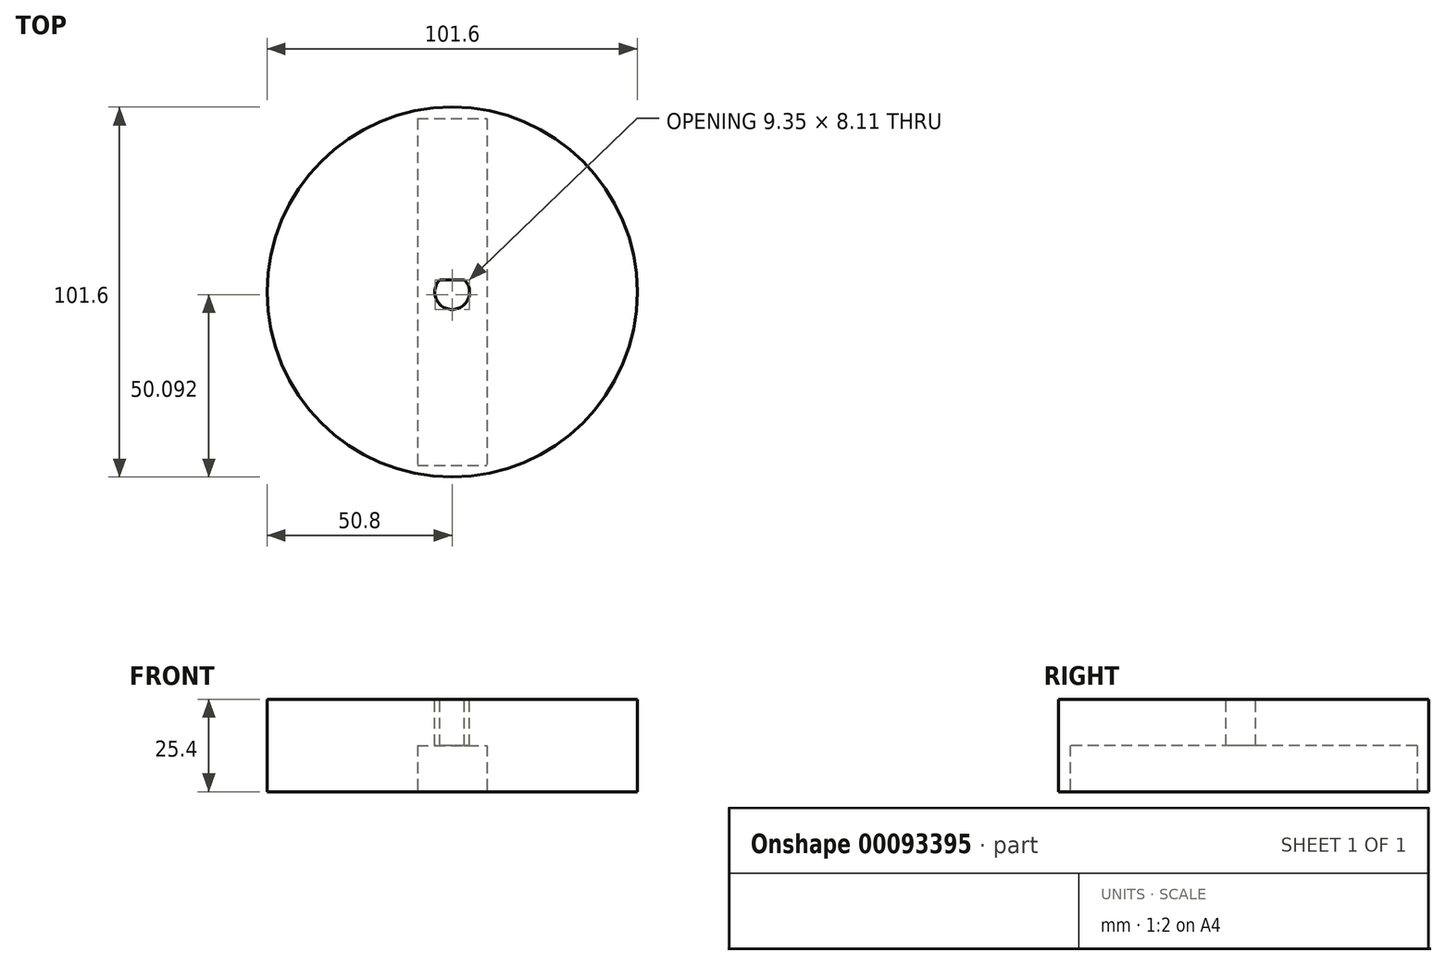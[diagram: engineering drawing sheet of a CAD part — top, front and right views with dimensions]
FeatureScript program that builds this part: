
annotation { "Feature Type Name" : "Feature", "Feature Type Description" : "" }
export const myFeature = defineFeature(function(context is Context, id is Id, definition is map)
    precondition{}
    {
        {
            var Q0;
            Q0=qCreatedBy(makeId("Top.planeOp"),FACE);
            var sketch = newSketch(context, id + "F0", { "sketchPlane" : qUnion([Q0])});
            skCircle(sketch, "E0", {"center": v(0, 0) * mm, "radius": 50.8 * mm});
            skSolve(sketch);
        }
        {
            var Q0;
            Q0 = qSketchRegion(id + "F0", true);
            extrude(context, id + "F1", {"entities" : qUnion([Q0]), "depth" : 25.4 * mm});
        }
        {
            var Q0;
            Q0=makeQuery(id+"F1.opExtrude","CAP_FACE",FACE,{"disambiguationData":[OSD([sQuery(id+"F0.wireOp",EDGE,"E0")])],"isStart":true});
            var sketch = newSketch(context, id + "F2", { "sketchPlane" : qUnion([Q0])});
            skLineSegment(sketch, "E1.bottom", {"start": v(-9.52, -47.63) * mm, "end": v(9.53, -47.63) * mm});
            skLineSegment(sketch, "E1.top", {"start": v(-9.52, 47.63) * mm, "end": v(9.53, 47.63) * mm});
            skLineSegment(sketch, "E1.left", {"start": v(-9.52, -47.63) * mm, "end": v(-9.52, 47.63) * mm});
            skLineSegment(sketch, "E1.right", {"start": v(9.53, -47.63) * mm, "end": v(9.53, 47.63) * mm});
            skPoint(sketch, "E1.middle", {"position": v(0, 0) * mm});
            skSolve(sketch);
        }
        {
            var Q0;
            Q0 = qSketchRegion(id + "F2", true);
            extrude(context, id + "F3", {"entities" : qUnion([Q0]), "operationType" : NewBodyOperationType.REMOVE, "oppositeDirection" : true, "depth" : 12.7 * mm});
        }
        {
            var Q0;
            Q0=makeQuery(id+"F1.opExtrude","CAP_FACE",FACE,{"disambiguationData":[OSD([sQuery(id+"F0.wireOp",EDGE,"E0")])],"isStart":false});
            var sketch = newSketch(context, id + "F4", { "sketchPlane" : qUnion([Q0])});
            skLineSegment(sketch, "E2", {"start": v(-3.39, 3.35) * mm, "end": v(3.39, 3.35) * mm});
            skArc(sketch, "E3", {"start": v(-3.39, 3.35) * mm, "mid": v(0, -4.76) * mm, "end": v(3.39, 3.35) * mm});
            skSolve(sketch);
        }
        {
            var Q0;
            Q0=makeQuery(id+"F4.imprint","IMPRINT",FACE,{"disambiguationData":[TD([[makeQuery(id+"F4.imprint","IMPRINT",EDGE,{"derivedFrom":sQuery(id+"F4.wireOp",EDGE,"E2")}),-1.0]])]});
            extrude(context, id + "F5", {"entities" : qUnion([Q0]), "operationType" : NewBodyOperationType.REMOVE, "oppositeDirection" : true, "depth" : 25.4 * mm});
        }
    });
